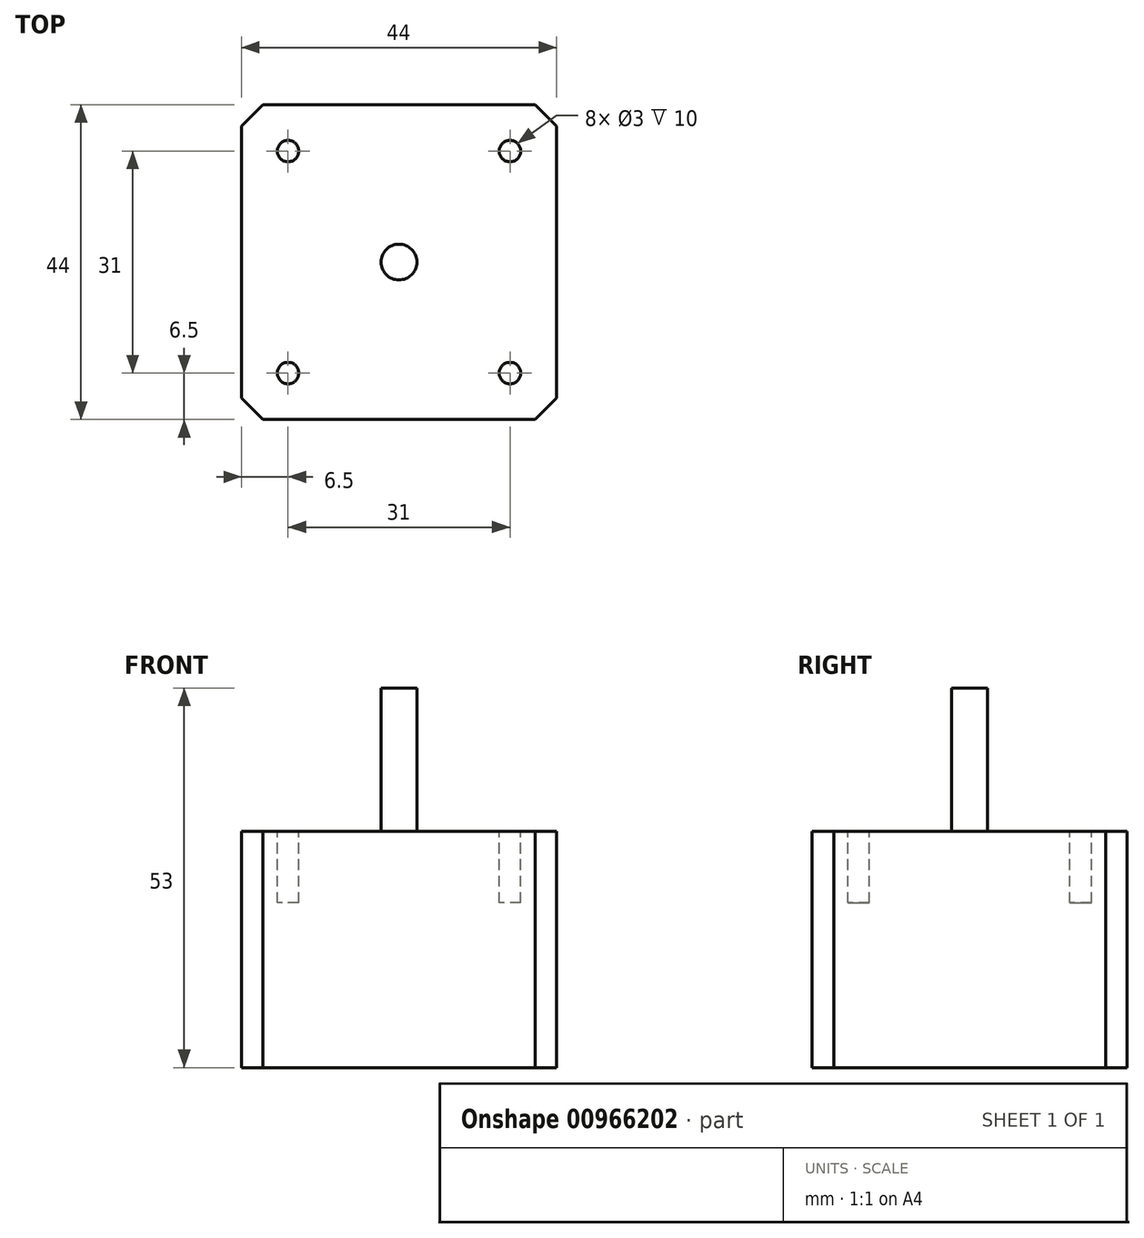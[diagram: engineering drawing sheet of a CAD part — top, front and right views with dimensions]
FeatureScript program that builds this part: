
annotation { "Feature Type Name" : "Feature", "Feature Type Description" : "" }
export const myFeature = defineFeature(function(context is Context, id is Id, definition is map)
    precondition{}
    {
        {
            var Q0;
            Q0=qCreatedBy(makeId("Top.planeOp"),FACE);
            var sketch = newSketch(context, id + "F0", { "sketchPlane" : qUnion([Q0])});
            skLineSegment(sketch, "E0.bottom", {"start": v(22, -22) * mm, "end": v(-22, -22) * mm});
            skLineSegment(sketch, "E0.top", {"start": v(22, 22) * mm, "end": v(-22, 22) * mm});
            skLineSegment(sketch, "E0.left", {"start": v(22, -22) * mm, "end": v(22, 22) * mm});
            skLineSegment(sketch, "E0.right", {"start": v(-22, -22) * mm, "end": v(-22, 22) * mm});
            skPoint(sketch, "E0.middle", {"position": v(0, 0) * mm});
            skCircle(sketch, "E1", {"center": v(0, 0) * mm, "radius": 2.5 * mm});
            skSolve(sketch);
        }
        {
            var Q0;
            Q0=qSketchRegion(id+"F0",true);
            extrude(context, id + "F1", {"entities" : qUnion([Q0]), "depth" : 33 * mm});
        }
        {
            var Q0;
            Q0=makeQuery(id+"F0.imprint","IMPRINT",FACE,{"disambiguationData":[TD([[makeQuery(id+"F0.imprint","IMPRINT",EDGE,{"derivedFrom":sQuery(id+"F0.wireOp",EDGE,"E1")}),1.0]])]});
            extrude(context, id + "F2", {"entities" : qUnion([Q0]), "operationType" : NewBodyOperationType.ADD, "depth" : 53 * mm});
        }
        {
            var Q0;
            Q0=makeQuery(id+"F1.opExtrude","SWEPT_EDGE",EDGE,{"disambiguationData":[OSD([sQuery(id+"F0.wireOp",EDGE,"E0.top"),sQuery(id+"F0.wireOp",EDGE,"E0.left")])]});
            var Q1;
            Q1=makeQuery(id+"F1.opExtrude","SWEPT_EDGE",EDGE,{"disambiguationData":[OSD([sQuery(id+"F0.wireOp",EDGE,"E0.bottom"),sQuery(id+"F0.wireOp",EDGE,"E0.left")])]});
            var Q2;
            Q2=makeQuery(id+"F1.opExtrude","SWEPT_EDGE",EDGE,{"disambiguationData":[OSD([sQuery(id+"F0.wireOp",EDGE,"E0.top"),sQuery(id+"F0.wireOp",EDGE,"E0.right")])]});
            var Q3;
            Q3=makeQuery(id+"F1.opExtrude","SWEPT_EDGE",EDGE,{"disambiguationData":[OSD([sQuery(id+"F0.wireOp",EDGE,"E0.bottom"),sQuery(id+"F0.wireOp",EDGE,"E0.right")])]});
            chamfer(context, id + "F3", {"entities" : qUnion([Q0, Q1, Q2, Q3]), "width" : 3 * mm, "tangentPropagation" : true});
        }
        {
            var Q0;
            Q0=makeQuery(id+"F1.opExtrude","CAP_FACE",FACE,{"disambiguationData":[OSD([sQuery(id+"F0.wireOp",EDGE,"E0.bottom"),sQuery(id+"F0.wireOp",EDGE,"E0.top"),sQuery(id+"F0.wireOp",EDGE,"E0.left"),sQuery(id+"F0.wireOp",EDGE,"E0.right"),sQuery(id+"F0.wireOp",EDGE,"E1")])],"isStart":false});
            var sketch = newSketch(context, id + "F4", { "sketchPlane" : qUnion([Q0])});
            skCircle(sketch, "E2", {"center": v(-15.5, 15.5) * mm, "radius": 1.5 * mm});
            skCircle(sketch, "E3", {"center": v(15.5, 15.5) * mm, "radius": 1.5 * mm});
            skCircle(sketch, "E4", {"center": v(15.5, -15.5) * mm, "radius": 1.5 * mm});
            skCircle(sketch, "E5", {"center": v(-15.5, -15.5) * mm, "radius": 1.5 * mm});
            skSolve(sketch);
        }
        {
            var Q0;
            Q0=qSketchRegion(id+"F4",true);
            extrude(context, id + "F5", {"entities" : qUnion([Q0]), "operationType" : NewBodyOperationType.REMOVE, "oppositeDirection" : true, "depth" : 10 * mm});
        }
        {
            var Q0;
            Q0=makeQuery(id+"F1.opExtrude","SWEPT_BODY",BODY,{"disambiguationData":[OSD([sQuery(id+"F0.wireOp",EDGE,"E0.bottom"),sQuery(id+"F0.wireOp",EDGE,"E0.top"),sQuery(id+"F0.wireOp",EDGE,"E0.left"),sQuery(id+"F0.wireOp",EDGE,"E0.right"),sQuery(id+"F0.wireOp",EDGE,"E1")])]});
            transform(context, id + "F6", {"entities" : qUnion([Q0]), "transformType" : TransformType.TRANSLATION_3D, "dx" : 0 * mm, "dy" : 0 * mm, "dz" : 0 * mm, "makeCopy" : true});
        }
    });
